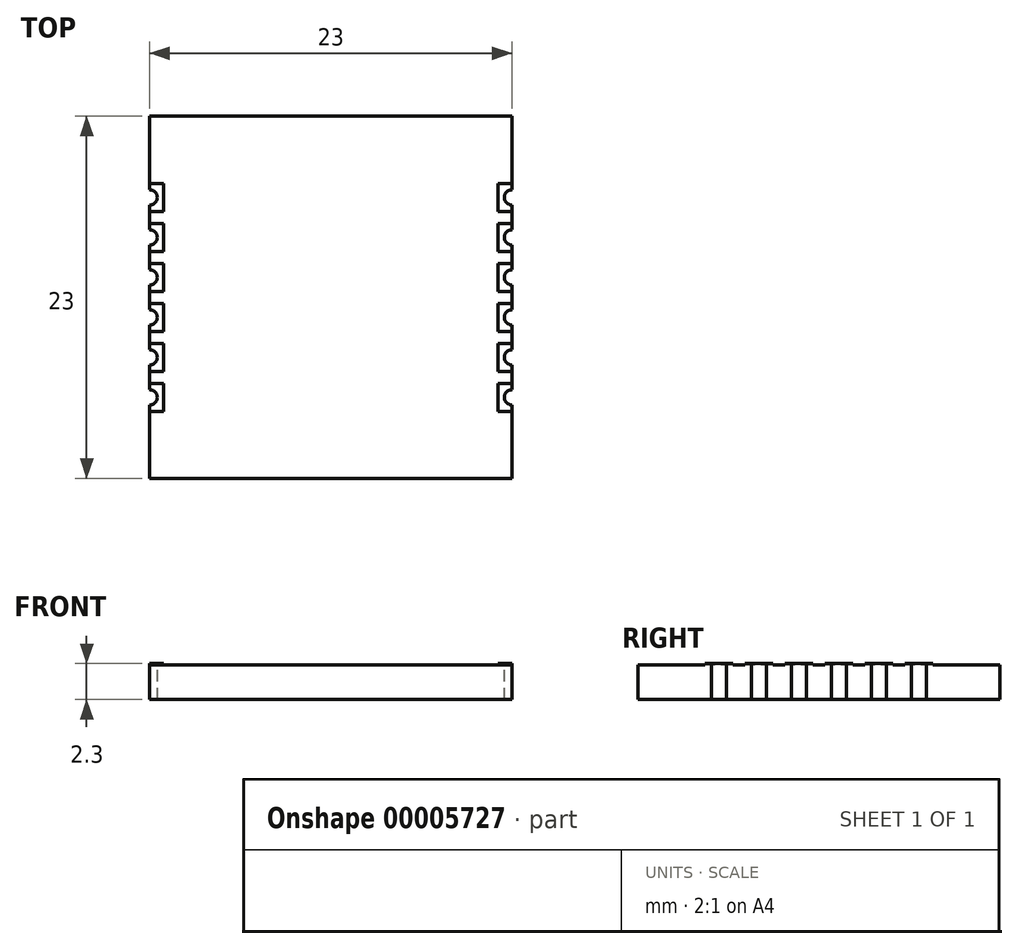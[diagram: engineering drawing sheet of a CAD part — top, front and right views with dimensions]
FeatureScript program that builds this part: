
annotation { "Feature Type Name" : "Feature", "Feature Type Description" : "" }
export const myFeature = defineFeature(function(context is Context, id is Id, definition is map)
    precondition{}
    {
        {
            var Q0;
            Q0=qCreatedBy(makeId("Top.planeOp"),FACE);
            var sketch = newSketch(context, id + "F0", { "sketchPlane" : qUnion([Q0])});
            skLineSegment(sketch, "E0.rect.bottom", {"start": v(11.5, 11.5) * mm, "end": v(-11.5, 11.5) * mm});
            skLineSegment(sketch, "E0.rect.top", {"start": v(11.5, -11.5) * mm, "end": v(-11.5, -11.5) * mm});
            skLineSegment(sketch, "E0.rect.left", {"start": v(11.5, 11.5) * mm, "end": v(11.5, -11.5) * mm});
            skLineSegment(sketch, "E0.rect.right", {"start": v(-11.5, 11.5) * mm, "end": v(-11.5, -11.5) * mm});
            skPoint(sketch, "E0.rect.middle", {"position": v(0, 0) * mm});
            skSolve(sketch);
        }
        {
            var Q0;
            Q0=makeQuery(id+"F0.imprint","IMPRINT",FACE,{"disambiguationData":[TD([[makeQuery(id+"F0.imprint","IMPRINT",EDGE,{"derivedFrom":sQuery(id+"F0.wireOp",EDGE,"E0.rect.bottom")}),1.0]])]});
            extrude(context, id + "F1", {"entities" : qUnion([Q0]), "depth" : 2.2 * mm});
        }
        {
            var Q0;
            Q0=makeQuery(id+"F1.opExtrude","CAP_FACE",FACE,{"disambiguationData":[OSD([sQuery(id+"F0.wireOp",EDGE,"E0.rect.bottom"),sQuery(id+"F0.wireOp",EDGE,"E0.rect.top"),sQuery(id+"F0.wireOp",EDGE,"E0.rect.left"),sQuery(id+"F0.wireOp",EDGE,"E0.rect.right")])],"isStart":false});
            var sketch = newSketch(context, id + "F2", { "sketchPlane" : qUnion([Q0])});
            skPoint(sketch, "E1", {"position": v(-11.5, -6.35) * mm});
            skCircle(sketch, "E2", {"center": v(-11.5, -6.35) * mm, "radius": 0.48 * mm});
            skCircle(sketch, "E3.0.1.0", {"center": v(-11.5, -3.8) * mm, "radius": 0.48 * mm});
            skCircle(sketch, "E3.0.2.0", {"center": v(-11.5, -1.27) * mm, "radius": 0.48 * mm});
            skCircle(sketch, "E3.0.3.0", {"center": v(-11.5, 1.27) * mm, "radius": 0.48 * mm});
            skCircle(sketch, "E3.0.4.0", {"center": v(-11.5, 3.81) * mm, "radius": 0.48 * mm});
            skCircle(sketch, "E3.0.5.0", {"center": v(-11.5, 6.35) * mm, "radius": 0.48 * mm});
            skCircle(sketch, "E3.1.0.0", {"center": v(11.5, -6.35) * mm, "radius": 0.48 * mm});
            skCircle(sketch, "E3.1.1.0", {"center": v(11.5, -3.8) * mm, "radius": 0.48 * mm});
            skCircle(sketch, "E3.1.2.0", {"center": v(11.5, -1.27) * mm, "radius": 0.48 * mm});
            skCircle(sketch, "E3.1.3.0", {"center": v(11.5, 1.27) * mm, "radius": 0.48 * mm});
            skCircle(sketch, "E3.1.4.0", {"center": v(11.5, 3.81) * mm, "radius": 0.48 * mm});
            skCircle(sketch, "E3.1.5.0", {"center": v(11.5, 6.35) * mm, "radius": 0.48 * mm});
            skLineSegment(sketch, "E3.direction1", {"start": v(-11.5, -6.35) * mm, "end": v(11.5, -6.35) * mm, "construction": true});
            skLineSegment(sketch, "E3.direction2", {"start": v(-11.5, -6.35) * mm, "end": v(-11.5, -3.8) * mm, "construction": true});
            skSolve(sketch);
        }
        {
            var Q0;
            {var subQ0=makeQuery(id+"F1.opExtrude","CAP_EDGE",EDGE,{"disambiguationData":[OSD([sQuery(id+"F0.wireOp",EDGE,"E0.rect.right")])],"isStart":false});var subQ1=sQuery(id+"F2.wireOp",EDGE,"E2");var subQ3=makeQuery(id+"F2.imprint","INTERSECT",VERTEX,{"disambiguationData":[OD(0.0)],"derivedFrom":[subQ0,subQ1]});Q0=makeQuery(id+"F2.imprint","IMPRINT",FACE,{"disambiguationData":[TD([[makeQuery(id+"F2.imprint","IMPRINT",EDGE,{"disambiguationData":[TD([[subQ3,1.0]])],"derivedFrom":subQ1}),1.0]])]});}
            var Q1;
            {var subQ0=makeQuery(id+"F1.opExtrude","CAP_EDGE",EDGE,{"disambiguationData":[OSD([sQuery(id+"F0.wireOp",EDGE,"E0.rect.right")])],"isStart":false});var subQ1=sQuery(id+"F2.wireOp",EDGE,"E3.0.1.0");var subQ3=makeQuery(id+"F2.imprint","INTERSECT",VERTEX,{"disambiguationData":[OD(0.0)],"derivedFrom":[subQ0,subQ1]});Q1=makeQuery(id+"F2.imprint","IMPRINT",FACE,{"disambiguationData":[TD([[makeQuery(id+"F2.imprint","IMPRINT",EDGE,{"disambiguationData":[TD([[subQ3,-1.0]])],"derivedFrom":subQ1}),1.0]])]});}
            var Q2;
            {var subQ0=makeQuery(id+"F1.opExtrude","CAP_EDGE",EDGE,{"disambiguationData":[OSD([sQuery(id+"F0.wireOp",EDGE,"E0.rect.right")])],"isStart":false});var subQ1=sQuery(id+"F2.wireOp",EDGE,"E3.0.2.0");var subQ3=makeQuery(id+"F2.imprint","INTERSECT",VERTEX,{"disambiguationData":[OD(0.0)],"derivedFrom":[subQ0,subQ1]});Q2=makeQuery(id+"F2.imprint","IMPRINT",FACE,{"disambiguationData":[TD([[makeQuery(id+"F2.imprint","IMPRINT",EDGE,{"disambiguationData":[TD([[subQ3,-1.0]])],"derivedFrom":subQ1}),1.0]])]});}
            var Q3;
            {var subQ0=makeQuery(id+"F1.opExtrude","CAP_EDGE",EDGE,{"disambiguationData":[OSD([sQuery(id+"F0.wireOp",EDGE,"E0.rect.right")])],"isStart":false});var subQ1=sQuery(id+"F2.wireOp",EDGE,"E3.0.3.0");var subQ3=makeQuery(id+"F2.imprint","INTERSECT",VERTEX,{"disambiguationData":[OD(0.0)],"derivedFrom":[subQ0,subQ1]});Q3=makeQuery(id+"F2.imprint","IMPRINT",FACE,{"disambiguationData":[TD([[makeQuery(id+"F2.imprint","IMPRINT",EDGE,{"disambiguationData":[TD([[subQ3,1.0]])],"derivedFrom":subQ1}),1.0]])]});}
            var Q4;
            {var subQ0=makeQuery(id+"F1.opExtrude","CAP_EDGE",EDGE,{"disambiguationData":[OSD([sQuery(id+"F0.wireOp",EDGE,"E0.rect.right")])],"isStart":false});var subQ1=sQuery(id+"F2.wireOp",EDGE,"E3.0.4.0");var subQ3=makeQuery(id+"F2.imprint","INTERSECT",VERTEX,{"disambiguationData":[OD(0.0)],"derivedFrom":[subQ0,subQ1]});Q4=makeQuery(id+"F2.imprint","IMPRINT",FACE,{"disambiguationData":[TD([[makeQuery(id+"F2.imprint","IMPRINT",EDGE,{"disambiguationData":[TD([[subQ3,1.0]])],"derivedFrom":subQ1}),1.0]])]});}
            var Q5;
            {var subQ0=makeQuery(id+"F1.opExtrude","CAP_EDGE",EDGE,{"disambiguationData":[OSD([sQuery(id+"F0.wireOp",EDGE,"E0.rect.right")])],"isStart":false});var subQ1=sQuery(id+"F2.wireOp",EDGE,"E3.0.5.0");var subQ3=makeQuery(id+"F2.imprint","INTERSECT",VERTEX,{"disambiguationData":[OD(0.0)],"derivedFrom":[subQ0,subQ1]});Q5=makeQuery(id+"F2.imprint","IMPRINT",FACE,{"disambiguationData":[TD([[makeQuery(id+"F2.imprint","IMPRINT",EDGE,{"disambiguationData":[TD([[subQ3,1.0]])],"derivedFrom":subQ1}),1.0]])]});}
            var Q6;
            {var subQ0=makeQuery(id+"F1.opExtrude","CAP_EDGE",EDGE,{"disambiguationData":[OSD([sQuery(id+"F0.wireOp",EDGE,"E0.rect.left")])],"isStart":false});var subQ1=sQuery(id+"F2.wireOp",EDGE,"E3.1.5.0");var subQ3=makeQuery(id+"F2.imprint","INTERSECT",VERTEX,{"disambiguationData":[OD(0.0)],"derivedFrom":[subQ0,subQ1]});Q6=makeQuery(id+"F2.imprint","IMPRINT",FACE,{"disambiguationData":[TD([[makeQuery(id+"F2.imprint","IMPRINT",EDGE,{"disambiguationData":[TD([[subQ3,-1.0]])],"derivedFrom":subQ1}),1.0]])]});}
            var Q7;
            {var subQ0=makeQuery(id+"F1.opExtrude","CAP_EDGE",EDGE,{"disambiguationData":[OSD([sQuery(id+"F0.wireOp",EDGE,"E0.rect.left")])],"isStart":false});var subQ1=sQuery(id+"F2.wireOp",EDGE,"E3.1.4.0");var subQ3=makeQuery(id+"F2.imprint","INTERSECT",VERTEX,{"disambiguationData":[OD(0.0)],"derivedFrom":[subQ0,subQ1]});Q7=makeQuery(id+"F2.imprint","IMPRINT",FACE,{"disambiguationData":[TD([[makeQuery(id+"F2.imprint","IMPRINT",EDGE,{"disambiguationData":[TD([[subQ3,-1.0]])],"derivedFrom":subQ1}),1.0]])]});}
            var Q8;
            {var subQ0=makeQuery(id+"F1.opExtrude","CAP_EDGE",EDGE,{"disambiguationData":[OSD([sQuery(id+"F0.wireOp",EDGE,"E0.rect.left")])],"isStart":false});var subQ1=sQuery(id+"F2.wireOp",EDGE,"E3.1.3.0");var subQ3=makeQuery(id+"F2.imprint","INTERSECT",VERTEX,{"disambiguationData":[OD(0.0)],"derivedFrom":[subQ0,subQ1]});Q8=makeQuery(id+"F2.imprint","IMPRINT",FACE,{"disambiguationData":[TD([[makeQuery(id+"F2.imprint","IMPRINT",EDGE,{"disambiguationData":[TD([[subQ3,-1.0]])],"derivedFrom":subQ1}),1.0]])]});}
            var Q9;
            {var subQ0=makeQuery(id+"F1.opExtrude","CAP_EDGE",EDGE,{"disambiguationData":[OSD([sQuery(id+"F0.wireOp",EDGE,"E0.rect.left")])],"isStart":false});var subQ1=sQuery(id+"F2.wireOp",EDGE,"E3.1.2.0");var subQ3=makeQuery(id+"F2.imprint","INTERSECT",VERTEX,{"disambiguationData":[OD(0.0)],"derivedFrom":[subQ0,subQ1]});Q9=makeQuery(id+"F2.imprint","IMPRINT",FACE,{"disambiguationData":[TD([[makeQuery(id+"F2.imprint","IMPRINT",EDGE,{"disambiguationData":[TD([[subQ3,1.0]])],"derivedFrom":subQ1}),1.0]])]});}
            var Q10;
            {var subQ0=makeQuery(id+"F1.opExtrude","CAP_EDGE",EDGE,{"disambiguationData":[OSD([sQuery(id+"F0.wireOp",EDGE,"E0.rect.left")])],"isStart":false});var subQ1=sQuery(id+"F2.wireOp",EDGE,"E3.1.1.0");var subQ3=makeQuery(id+"F2.imprint","INTERSECT",VERTEX,{"disambiguationData":[OD(0.0)],"derivedFrom":[subQ0,subQ1]});Q10=makeQuery(id+"F2.imprint","IMPRINT",FACE,{"disambiguationData":[TD([[makeQuery(id+"F2.imprint","IMPRINT",EDGE,{"disambiguationData":[TD([[subQ3,1.0]])],"derivedFrom":subQ1}),1.0]])]});}
            var Q11;
            {var subQ0=makeQuery(id+"F1.opExtrude","CAP_EDGE",EDGE,{"disambiguationData":[OSD([sQuery(id+"F0.wireOp",EDGE,"E0.rect.left")])],"isStart":false});var subQ1=sQuery(id+"F2.wireOp",EDGE,"E3.1.0.0");var subQ3=makeQuery(id+"F2.imprint","INTERSECT",VERTEX,{"disambiguationData":[OD(0.0)],"derivedFrom":[subQ0,subQ1]});Q11=makeQuery(id+"F2.imprint","IMPRINT",FACE,{"disambiguationData":[TD([[makeQuery(id+"F2.imprint","IMPRINT",EDGE,{"disambiguationData":[TD([[subQ3,1.0]])],"derivedFrom":subQ1}),1.0]])]});}
            var Q12;
            {var subQ0=makeQuery(id+"F1.opExtrude","CAP_EDGE",EDGE,{"disambiguationData":[OSD([sQuery(id+"F0.wireOp",EDGE,"E0.rect.right")])],"isStart":false});var subQ1=sQuery(id+"F2.wireOp",EDGE,"E2");var subQ3=makeQuery(id+"F2.imprint","INTERSECT",VERTEX,{"disambiguationData":[OD(0.0)],"derivedFrom":[subQ0,subQ1]});Q12=makeQuery(id+"F2.imprint","IMPRINT",FACE,{"disambiguationData":[TD([[makeQuery(id+"F2.imprint","IMPRINT",EDGE,{"disambiguationData":[TD([[subQ3,-1.0]])],"derivedFrom":subQ1}),1.0]])]});}
            extrude(context, id + "F3", {"entities" : qUnion([Q0, Q1, Q2, Q3, Q4, Q5, Q6, Q7, Q8, Q9, Q10, Q11, Q12]), "operationType" : NewBodyOperationType.REMOVE, "endBound" : BoundingType.THROUGH_ALL, "oppositeDirection" : true, "depth" : 25 * mm});
        }
        {
            var Q0;
            Q0=makeQuery(id+"F1.opExtrude","CAP_FACE",FACE,{"disambiguationData":[OSD([sQuery(id+"F0.wireOp",EDGE,"E0.rect.bottom"),sQuery(id+"F0.wireOp",EDGE,"E0.rect.top"),sQuery(id+"F0.wireOp",EDGE,"E0.rect.left"),sQuery(id+"F0.wireOp",EDGE,"E0.rect.right")])],"isStart":false});
            var sketch = newSketch(context, id + "F4", { "sketchPlane" : qUnion([Q0])});
            skPoint(sketch, "E4", {"position": v(-11.5, -6.35) * mm});
            skLineSegment(sketch, "E5.rect.bottom", {"start": v(-10.6, -5.46) * mm, "end": v(-12.39, -5.46) * mm});
            skLineSegment(sketch, "E5.rect.top", {"start": v(-10.6, -7.24) * mm, "end": v(-12.39, -7.24) * mm});
            skLineSegment(sketch, "E5.rect.left", {"start": v(-10.6, -5.46) * mm, "end": v(-10.6, -7.24) * mm});
            skLineSegment(sketch, "E5.rect.right", {"start": v(-12.39, -5.46) * mm, "end": v(-12.39, -7.24) * mm});
            skLineSegment(sketch, "E6.0.1.0", {"start": v(-10.6, -2.92) * mm, "end": v(-12.39, -2.92) * mm});
            skLineSegment(sketch, "E6.0.1.1", {"start": v(-10.6, -2.92) * mm, "end": v(-10.6, -4.7) * mm});
            skLineSegment(sketch, "E6.0.1.2", {"start": v(-10.6, -4.7) * mm, "end": v(-12.39, -4.7) * mm});
            skLineSegment(sketch, "E6.0.1.3", {"start": v(-12.39, -2.92) * mm, "end": v(-12.39, -4.7) * mm});
            skLineSegment(sketch, "E6.0.2.0", {"start": v(-10.6, -0.38) * mm, "end": v(-12.39, -0.38) * mm});
            skLineSegment(sketch, "E6.0.2.1", {"start": v(-10.6, -0.38) * mm, "end": v(-10.6, -2.16) * mm});
            skLineSegment(sketch, "E6.0.2.2", {"start": v(-10.6, -2.16) * mm, "end": v(-12.39, -2.16) * mm});
            skLineSegment(sketch, "E6.0.2.3", {"start": v(-12.39, -0.38) * mm, "end": v(-12.39, -2.16) * mm});
            skLineSegment(sketch, "E6.0.3.0", {"start": v(-10.6, 2.16) * mm, "end": v(-12.39, 2.16) * mm});
            skLineSegment(sketch, "E6.0.3.1", {"start": v(-10.6, 2.16) * mm, "end": v(-10.6, 0.38) * mm});
            skLineSegment(sketch, "E6.0.3.2", {"start": v(-10.6, 0.38) * mm, "end": v(-12.39, 0.38) * mm});
            skLineSegment(sketch, "E6.0.3.3", {"start": v(-12.39, 2.16) * mm, "end": v(-12.39, 0.38) * mm});
            skLineSegment(sketch, "E6.0.4.0", {"start": v(-10.6, 4.7) * mm, "end": v(-12.39, 4.7) * mm});
            skLineSegment(sketch, "E6.0.4.1", {"start": v(-10.6, 4.7) * mm, "end": v(-10.6, 2.92) * mm});
            skLineSegment(sketch, "E6.0.4.2", {"start": v(-10.6, 2.92) * mm, "end": v(-12.39, 2.92) * mm});
            skLineSegment(sketch, "E6.0.4.3", {"start": v(-12.39, 4.7) * mm, "end": v(-12.39, 2.92) * mm});
            skLineSegment(sketch, "E6.0.5.0", {"start": v(-10.6, 7.24) * mm, "end": v(-12.39, 7.24) * mm});
            skLineSegment(sketch, "E6.0.5.1", {"start": v(-10.6, 7.24) * mm, "end": v(-10.6, 5.46) * mm});
            skLineSegment(sketch, "E6.0.5.2", {"start": v(-10.6, 5.46) * mm, "end": v(-12.39, 5.46) * mm});
            skLineSegment(sketch, "E6.0.5.3", {"start": v(-12.39, 7.24) * mm, "end": v(-12.39, 5.46) * mm});
            skLineSegment(sketch, "E6.1.0.0", {"start": v(12.4, -5.46) * mm, "end": v(10.61, -5.46) * mm});
            skLineSegment(sketch, "E6.1.0.1", {"start": v(12.4, -5.46) * mm, "end": v(12.4, -7.24) * mm});
            skLineSegment(sketch, "E6.1.0.2", {"start": v(12.4, -7.24) * mm, "end": v(10.61, -7.24) * mm});
            skLineSegment(sketch, "E6.1.0.3", {"start": v(10.61, -5.46) * mm, "end": v(10.61, -7.24) * mm});
            skLineSegment(sketch, "E6.1.1.0", {"start": v(12.4, -2.92) * mm, "end": v(10.61, -2.92) * mm});
            skLineSegment(sketch, "E6.1.1.1", {"start": v(12.4, -2.92) * mm, "end": v(12.4, -4.7) * mm});
            skLineSegment(sketch, "E6.1.1.2", {"start": v(12.4, -4.7) * mm, "end": v(10.61, -4.7) * mm});
            skLineSegment(sketch, "E6.1.1.3", {"start": v(10.61, -2.92) * mm, "end": v(10.61, -4.7) * mm});
            skLineSegment(sketch, "E6.1.2.0", {"start": v(12.4, -0.38) * mm, "end": v(10.61, -0.38) * mm});
            skLineSegment(sketch, "E6.1.2.1", {"start": v(12.4, -0.38) * mm, "end": v(12.4, -2.16) * mm});
            skLineSegment(sketch, "E6.1.2.2", {"start": v(12.4, -2.16) * mm, "end": v(10.61, -2.16) * mm});
            skLineSegment(sketch, "E6.1.2.3", {"start": v(10.61, -0.38) * mm, "end": v(10.61, -2.16) * mm});
            skLineSegment(sketch, "E6.1.3.0", {"start": v(12.4, 2.16) * mm, "end": v(10.61, 2.16) * mm});
            skLineSegment(sketch, "E6.1.3.1", {"start": v(12.4, 2.16) * mm, "end": v(12.4, 0.38) * mm});
            skLineSegment(sketch, "E6.1.3.2", {"start": v(12.4, 0.38) * mm, "end": v(10.61, 0.38) * mm});
            skLineSegment(sketch, "E6.1.3.3", {"start": v(10.61, 2.16) * mm, "end": v(10.61, 0.38) * mm});
            skLineSegment(sketch, "E6.1.4.0", {"start": v(12.4, 4.7) * mm, "end": v(10.61, 4.7) * mm});
            skLineSegment(sketch, "E6.1.4.1", {"start": v(12.4, 4.7) * mm, "end": v(12.4, 2.92) * mm});
            skLineSegment(sketch, "E6.1.4.2", {"start": v(12.4, 2.92) * mm, "end": v(10.61, 2.92) * mm});
            skLineSegment(sketch, "E6.1.4.3", {"start": v(10.61, 4.7) * mm, "end": v(10.61, 2.92) * mm});
            skLineSegment(sketch, "E6.1.5.0", {"start": v(12.4, 7.24) * mm, "end": v(10.61, 7.24) * mm});
            skLineSegment(sketch, "E6.1.5.1", {"start": v(12.4, 7.24) * mm, "end": v(12.4, 5.46) * mm});
            skLineSegment(sketch, "E6.1.5.2", {"start": v(12.4, 5.46) * mm, "end": v(10.61, 5.46) * mm});
            skLineSegment(sketch, "E6.1.5.3", {"start": v(10.61, 7.24) * mm, "end": v(10.61, 5.46) * mm});
            skLineSegment(sketch, "E6.direction1", {"start": v(-12.39, -5.46) * mm, "end": v(10.61, -5.46) * mm, "construction": true});
            skLineSegment(sketch, "E6.direction2", {"start": v(-12.39, -5.46) * mm, "end": v(-12.39, -2.92) * mm, "construction": true});
            skSolve(sketch);
        }
        {
            var Q0;
            {var subQ15=sQuery(id+"F4.wireOp",EDGE,"E5.rect.left");Q0=makeQuery(id+"F4.imprint","IMPRINT",FACE,{"disambiguationData":[TD([[makeQuery(id+"F4.imprint","IMPRINT",EDGE,{"derivedFrom":subQ15}),-1.0]])]});}
            var Q1;
            {var subQ14=sQuery(id+"F4.wireOp",EDGE,"E6.0.5.1");Q1=makeQuery(id+"F4.imprint","IMPRINT",FACE,{"disambiguationData":[TD([[makeQuery(id+"F4.imprint","IMPRINT",EDGE,{"derivedFrom":subQ14}),-1.0]])]});}
            var Q2;
            {var subQ13=sQuery(id+"F4.wireOp",EDGE,"E6.0.4.1");Q2=makeQuery(id+"F4.imprint","IMPRINT",FACE,{"disambiguationData":[TD([[makeQuery(id+"F4.imprint","IMPRINT",EDGE,{"derivedFrom":subQ13}),-1.0]])]});}
            var Q3;
            {var subQ13=sQuery(id+"F4.wireOp",EDGE,"E6.0.3.1");Q3=makeQuery(id+"F4.imprint","IMPRINT",FACE,{"disambiguationData":[TD([[makeQuery(id+"F4.imprint","IMPRINT",EDGE,{"derivedFrom":subQ13}),-1.0]])]});}
            var Q4;
            {var subQ13=sQuery(id+"F4.wireOp",EDGE,"E6.0.2.1");Q4=makeQuery(id+"F4.imprint","IMPRINT",FACE,{"disambiguationData":[TD([[makeQuery(id+"F4.imprint","IMPRINT",EDGE,{"derivedFrom":subQ13}),-1.0]])]});}
            var Q5;
            {var subQ13=sQuery(id+"F4.wireOp",EDGE,"E6.0.1.1");Q5=makeQuery(id+"F4.imprint","IMPRINT",FACE,{"disambiguationData":[TD([[makeQuery(id+"F4.imprint","IMPRINT",EDGE,{"derivedFrom":subQ13}),-1.0]])]});}
            var Q6;
            {var subQ10=sQuery(id+"F4.wireOp",EDGE,"E6.1.1.3");Q6=makeQuery(id+"F4.imprint","IMPRINT",FACE,{"disambiguationData":[TD([[makeQuery(id+"F4.imprint","IMPRINT",EDGE,{"derivedFrom":subQ10}),1.0]])]});}
            var Q7;
            {var subQ14=sQuery(id+"F4.wireOp",EDGE,"E6.1.0.3");Q7=makeQuery(id+"F4.imprint","IMPRINT",FACE,{"disambiguationData":[TD([[makeQuery(id+"F4.imprint","IMPRINT",EDGE,{"derivedFrom":subQ14}),1.0]])]});}
            var Q8;
            {var subQ13=sQuery(id+"F4.wireOp",EDGE,"E6.1.2.3");Q8=makeQuery(id+"F4.imprint","IMPRINT",FACE,{"disambiguationData":[TD([[makeQuery(id+"F4.imprint","IMPRINT",EDGE,{"derivedFrom":subQ13}),1.0]])]});}
            var Q9;
            {var subQ13=sQuery(id+"F4.wireOp",EDGE,"E6.1.3.3");Q9=makeQuery(id+"F4.imprint","IMPRINT",FACE,{"disambiguationData":[TD([[makeQuery(id+"F4.imprint","IMPRINT",EDGE,{"derivedFrom":subQ13}),1.0]])]});}
            var Q10;
            {var subQ13=sQuery(id+"F4.wireOp",EDGE,"E6.1.4.3");Q10=makeQuery(id+"F4.imprint","IMPRINT",FACE,{"disambiguationData":[TD([[makeQuery(id+"F4.imprint","IMPRINT",EDGE,{"derivedFrom":subQ13}),1.0]])]});}
            var Q11;
            {var subQ11=sQuery(id+"F4.wireOp",EDGE,"E6.1.5.3");Q11=makeQuery(id+"F4.imprint","IMPRINT",FACE,{"disambiguationData":[TD([[makeQuery(id+"F4.imprint","IMPRINT",EDGE,{"derivedFrom":subQ11}),1.0]])]});}
            extrude(context, id + "F5", {"entities" : qUnion([Q0, Q1, Q2, Q3, Q4, Q5, Q6, Q7, Q8, Q9, Q10, Q11]), "operationType" : NewBodyOperationType.ADD, "depth" : 0.1 * mm});
        }
    });
